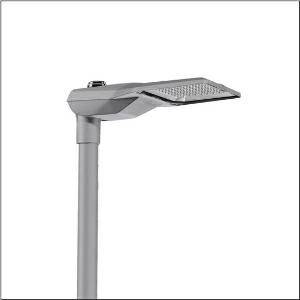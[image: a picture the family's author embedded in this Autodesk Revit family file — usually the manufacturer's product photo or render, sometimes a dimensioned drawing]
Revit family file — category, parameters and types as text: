
# Revit family: streetlight_sl_21_midi___st1_0a_5xe7d67n08mb_a1db
name_source: partatom
category: Lighting Fixtures
units: mm (PartAtom-declared; Revit-internal decimal feet)

## family parameters
Cut with Voids When Loaded = No
Host = Face
Light Source = No
Part Type = Normal
Room Calculation Point = No
Round Connector Dimension = Use Diameter
Shared = No

## types (1)
- --- (1 x LED, 16240 lm, 134.3 W, 2700K)
    Apparent Load = 134 VA
    CIE Flux Codes = 37 72 97 100 100
    Color Rendering = 70
    Color Temperature = 2700K
    Default Elevation = 1800 mm
    Description = Streetlight SL 21 midi, mast luminaire, primary light control with lens, of PMMA, primary optical cover: cover, of toughened safety glass, transparent, light distribution: ST1.0a, light emission: direct distribution, primary light characteristic: asymmetric, installation type: side-entry, LED, 3G 2.5mm², High Power LED, rated luminous flux: 16.240lm, luminous efficacy: 121lm/W, light colour: 727, colour temperature: 2700K, control: overheat protection, presetting dimming linear, constant luminous flux control, time-dependent luminous flux control, flexible luminous flux parameterisation, mains connection: 220..240V, AC, 50/60Hz, connection cable pre-assembled, cable length: 12,5m, wiring characteristics: H05VV-F, start of lifetime: 134W, end of service life: 141W, reduction: 60W, luminaire housing, of diecast aluminium (EN AC-44300), powder-coated, Siteco® metallic grey (DB 702S), corrosivity category C5 mid according to DIN EN ISO 12944, multi-level sealing system, sealing non-destructively replaceable, inclination adjustable: 0°, 5°, 10°, 15°, length: 644mm, width: 335mm, height: 110mm, spigot size: 42mm (side-entry), protection rating (complete): IP66, insulation class (complete): insulation class I (protective earthing), certification: CE, ENEC, ENEC+, VDE, impact resistance: IK09, permissible operating ambient temperature for outdoor applications: -40..+50°C, standard-compliant lighting for roads and squares, packaging unit: 1 piece

Light Distribution: ST1.0a
    Height = 111 mm
    Lamp = 1 x LED
    Lamp Light Flux = 16240 lm
    Lamp Power = 134.3 W
    Lamp count = 1
    Length = 644 mm
    Luminous efficacy = 121 lm/W
    Manufacturer = Siteco
    ModVariant = No
    Model = 5XE7D67N08MB
    Number of Poles = 1
    OnlyDefault = Yes
    Power Factor = 1
    Product Name = Streetlight SL 21 midi | ST1.0a
    Product group = mast luminaire | pylon top
    ProductGroupID = 6100
    Protection Class = Protection class I
    Protection Degree = IP 66
    RLX_Detail_Level = 1
    RLX_Emergency_Light_Flux = 0 lm
    RLX_Emergency_Type = 0
    RLX_Emergency_Type_DB = No
    RlxData = <blob elided: 90085 chars, md5=5e73cb5c>
    Socket = socket
    Standby Power = 0 W
    System Light Flux = 16240 lm
    System Power = 134 W
    Type Comments = factory setting: luminous flux: 100 % | dim-lin: 254 | 687 mA
    Type Image = l_1294377.jpg
    URL = http://relux.com
    VarID = @adj_085271
    Voltage = 0 V
    Weight = 0.00 kg
    Width = 336 mm

## geometry (parser evidence)
native form markers: Blend x4, Sweep x11
no freeform markers — native parametric forms only
